# Revit family: 2CKA001761A1490
name_source: partatom
category: Elektroinstallationen
revit_build: Autodesk Revit 2017 (Build: 20160225_1515(x64)
units: mm (PartAtom-declared; Revit-internal decimal feet)

## family parameters
Basisbauteil = Fläche
Beim Laden mit Abzugskörper schneiden = Nein
Bemaßung runder Anschluss = Durchmesser verwenden
Beschriftungsausrichtung beibehalten = Nein
Gemeinsam genutzt = Nein
Raumberechnungspunkt = Nein
Teiletyp = Normal

## types (1)
- 2CKA001761A1490
    BIM = https://media.live.bim.site
    BIMSITE_PRODUCT_ID = 21f05d8b9b9f280c7dcc9dc7d715ed204f75efaf
    Beschreibung = Leitungsdurchführung, blaugrün, Aufputz IP 44, Zubehör ocean und Sondergeräte, Leitungsdurchführung Verbindungsstück zum Koppeln mehrerer Geräte Schutzart Gerät: IP 44
    Datenblatt = https://media.live.bim.site
    Farbe = blaugrün
    GTIN = 4011395993057
    Gerätebreite [mm] = 67
    Gerätehöhe [mm] = 16
    Gerätetiefe [mm] = 24
    Gewicht [kg/m] = 0.008
    HAN = 2CKA001761A1490
    HeinzeBIM = https://www.heinze.de
    Hersteller = Busch-Jaeger
    Ist System = Nein
    Ist Zubehör = Nein
    Produktseite = https://media.live.bim.site
    TYPE = 2138 W-53
    Typname = Leitungsdurchführung, blaugrün, Aufputz IP 44, Zubehör ocean und Sondergeräte
    URL = https://www.busch-jaeger.de
    Vorgabe-Ansicht = 1219 mm

## geometry (parser evidence)
native form markers: Sweep x3
no freeform markers — native parametric forms only
